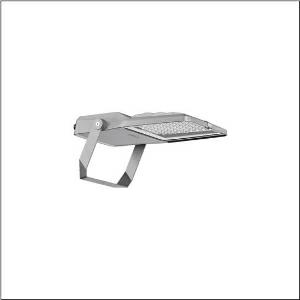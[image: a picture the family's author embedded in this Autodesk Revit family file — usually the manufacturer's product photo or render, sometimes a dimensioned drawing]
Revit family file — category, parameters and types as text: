
# Revit family: floodlight_fl_21_iq_mini___pl61_5xa7772d1c1a_27aa
name_source: partatom
category: Lighting Fixtures
units: mm (PartAtom-declared; Revit-internal decimal feet)

## family parameters
Cut with Voids When Loaded = No
Host = Face
Light Source = No
Part Type = Normal
Room Calculation Point = No
Round Connector Dimension = Use Diameter
Shared = No

## types (1)
- --- (1 x LED, 14490 lm, 143 W, 2200K)
    Apparent Load = 143 VA
    CIE Flux Codes = 33 65 98 100 100
    Color Rendering = 70
    Color Temperature = 2200K
    Default Elevation = 1800 mm
    Description = Floodlight FL 21 iQ mini, floodlight, primary light control with lens, of PMMA, primary optical cover: protective disc, of toughened safety glass, transparent, light distribution: PL61, light emission: direct distribution, installation type: surface-mounted, LED, High Power LED, rated luminous flux: 14.490lm, luminous efficacy: 101lm/W, light colour: 722, colour temperature: 2200K, control gear: iQ Street-Remote/DALI, control: Street-Remote, Auto-Match, Temp-Guard, Night-Set, Smart-Wire, Desk-Remote (wireless, voltage-free reading and setting of iQ features in the workshop via application-optimized NFC function/RFID function), optimised constant luminous flux control (CLO 2.0), with terminal, 6-pole, mains connection: 220..240V, AC, 50/60Hz, start of lifetime: 143W, end of service life: 152W, reduction: 61W, luminaire housing, of diecast aluminium, powder-coated, Siteco® metallic grey (DB 702S), corrosivity category C5 mid according to DIN EN ISO 12944, suitable for swimming pools, chlorine-resistant, sealing non-destructively replaceable, mounting bracket, of steel, galvanised, powder-coated, Siteco® metallic grey (DB 702S), protection rating (complete): IP66, insulation class (complete): insulation class II (safety insulation), certification: CE, ENEC, VDE, protection symbol: D, impact resistance: IK08, permissible operating ambient temperature: -40..+40°C, permissible operating ambient temperature for outdoor applications: -40..+50°C, standard: DIN EN 12944, LABS conformity tested according to VDMA 24364:2018-05, packaging unit: 1 piece

Light Distribution: PL61
    Height = 70 mm
    Lamp = 1 x LED
    Lamp Light Flux = 14490 lm
    Lamp Power = 143 W
    Lamp count = 1
    Length = 485 mm
    Luminous efficacy = 101 lm/W
    Manufacturer = Siteco
    ModVariant = No
    Model = 5XA7772D1C1A
    Number of Poles = 1
    OnlyDefault = Yes
    Power Factor = 1
    Product Name = Floodlight FL 21 iQ mini | PL61
    Product group = floodlight | pylon annexe
    ProductGroupID = 6200
    Protection Class = Protection class II
    Protection Degree = IP 66
    RLX_Detail_Level = 1
    RLX_Emergency_Light_Flux = 0 lm
    RLX_Emergency_Type = 0
    RLX_Emergency_Type_DB = No
    RlxData = <blob elided: 96781 chars, md5=e676d4de>
    Socket = socket
    Standby Power = 0 W
    System Light Flux = 14490 lm
    System Power = 143 W
    Type Comments = factory setting: luminous flux: 100 % | dim-lin: 254 | 730 mA
    Type Image = l_1006845.jpg
    URL = http://relux.com
    VarID = @adj_172566
    Voltage = 0 V
    Weight = 0.00 kg
    Width = 337 mm

## geometry (parser evidence)
native form markers: Blend x4, Sweep x14
no freeform markers — native parametric forms only
